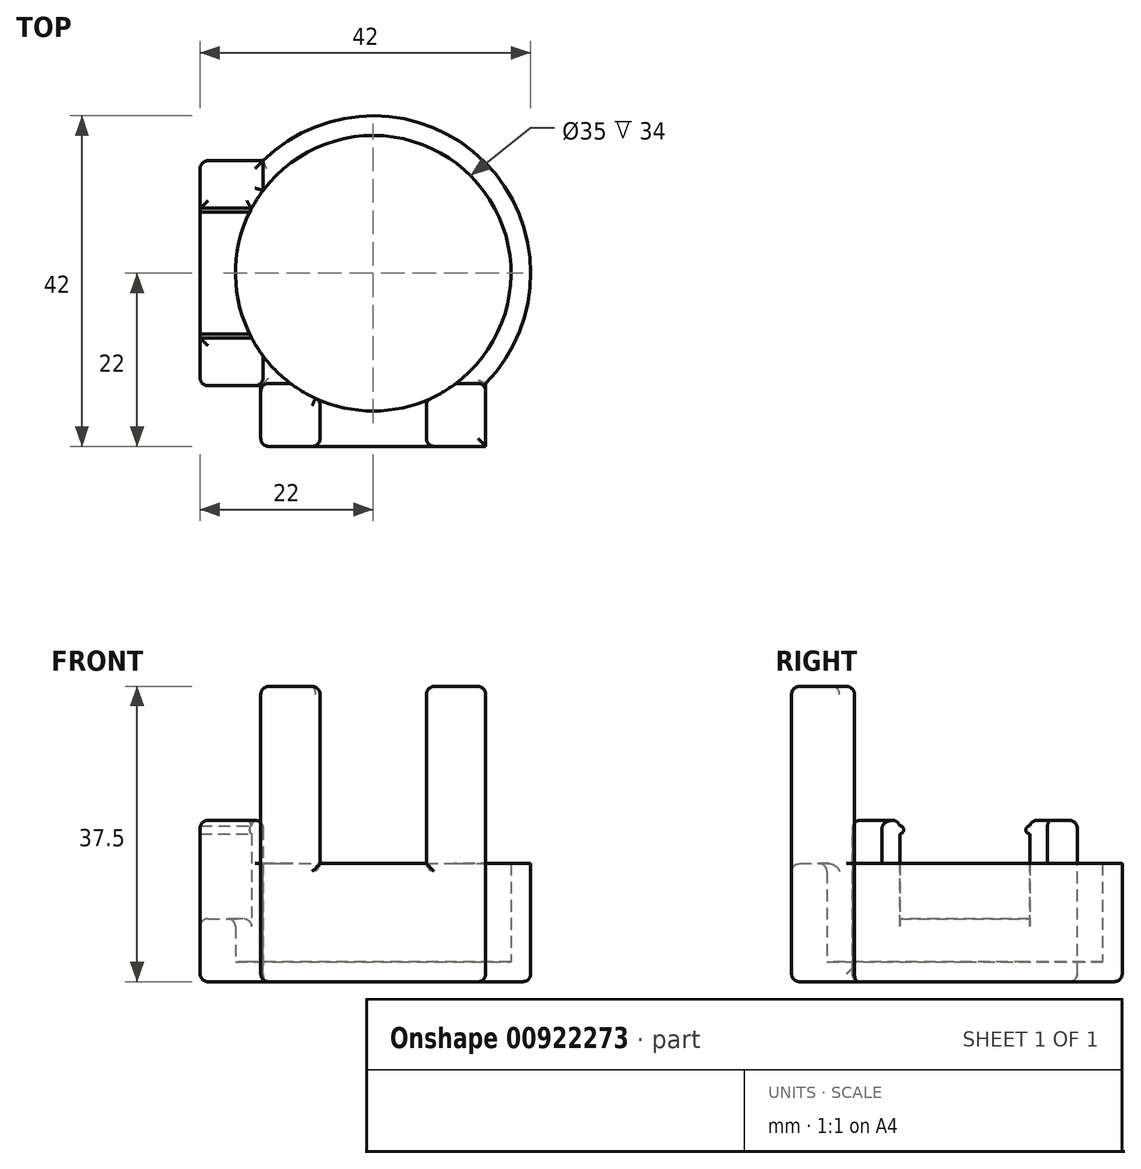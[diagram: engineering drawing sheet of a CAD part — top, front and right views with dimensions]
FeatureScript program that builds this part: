
annotation { "Feature Type Name" : "Feature", "Feature Type Description" : "" }
export const myFeature = defineFeature(function(context is Context, id is Id, definition is map)
    precondition{}
    {
        {
            var Q0;
            Q0=qCreatedBy(makeId("Top.planeOp"),FACE);
            var sketch = newSketch(context, id + "F0", { "sketchPlane" : qUnion([Q0])});
            skCircle(sketch, "E0", {"center": v(0, 0) * mm, "radius": 20 * mm});
            skSolve(sketch);
        }
        {
            var Q0;
            Q0=qSketchRegion(id+"F0",true);
            extrude(context, id + "F1", {"entities" : qUnion([Q0]), "depth" : 18 * mm, "offsetDistance" : 25 * mm});
        }
        {
            var Q0;
            Q0=makeQuery(id+"F1.opExtrude","CAP_FACE",FACE,{"disambiguationData":[OSD([sQuery(id+"F0.wireOp",EDGE,"E0")])],"isStart":true});
            extrude(context, id + "F2", {"entities" : qUnion([Q0]), "operationType" : NewBodyOperationType.ADD, "depth" : 2.5 * mm, "offsetDistance" : 25 * mm});
        }
        {
            var Q0;
            Q0=qCreatedBy(makeId("Top.planeOp"),FACE);
            var sketch = newSketch(context, id + "F3", { "sketchPlane" : qUnion([Q0])});
            skCircle(sketch, "E1", {"center": v(0, 0) * mm, "radius": 17.5 * mm});
            skSolve(sketch);
        }
        {
            var Q0;
            Q0=qCreatedBy(makeId("Front.planeOp"),FACE);
            var sketch = newSketch(context, id + "F4", { "sketchPlane" : qUnion([Q0])});
            skLineSegment(sketch, "E2.bottom", {"start": v(26, 12.5) * mm, "end": v(-14, 12.5) * mm});
            skLineSegment(sketch, "E2.top", {"start": v(26, 62.5) * mm, "end": v(-14, 62.5) * mm});
            skLineSegment(sketch, "E2.left", {"start": v(26, 12.5) * mm, "end": v(26, 62.5) * mm});
            skLineSegment(sketch, "E2.right", {"start": v(-14, 12.5) * mm, "end": v(-14, 62.5) * mm});
            skSolve(sketch);
        }
        {
            var Q0;
            Q0=qSketchRegion(id+"F4",true);
            extrude(context, id + "F5", {"entities" : qUnion([Q0]), "operationType" : NewBodyOperationType.REMOVE, "endBound" : BoundingType.SYMMETRIC, "depth" : 50 * mm, "offsetDistance" : 25 * mm});
        }
        {
            var Q0;
            Q0=qCreatedBy(makeId("Top.planeOp"),FACE);
            var sketch = newSketch(context, id + "F6", { "sketchPlane" : qUnion([Q0])});
            skLineSegment(sketch, "E3.bottom", {"start": v(-14, 14.28) * mm, "end": v(-22, 14.28) * mm});
            skLineSegment(sketch, "E3.top", {"start": v(-14, -14.28) * mm, "end": v(-22, -14.28) * mm});
            skLineSegment(sketch, "E3.left", {"start": v(-14, 14.28) * mm, "end": v(-14, -14.28) * mm});
            skLineSegment(sketch, "E3.right", {"start": v(-22, 14.28) * mm, "end": v(-22, -14.28) * mm});
            skSolve(sketch);
        }
        {
            var Q0;
            Q0=qSketchRegion(id+"F6",true);
            extrude(context, id + "F7", {"entities" : qUnion([Q0]), "operationType" : NewBodyOperationType.ADD, "oppositeDirection" : true, "depth" : 2.5 * mm, "offsetDistance" : 25 * mm});
        }
        {
            var Q0;
            Q0=qSketchRegion(id+"F6",true);
            extrude(context, id + "F8", {"entities" : qUnion([Q0]), "operationType" : NewBodyOperationType.ADD, "depth" : 18 * mm, "offsetDistance" : 25 * mm});
        }
        {
            var Q0;
            Q0=qCreatedBy(makeId("Top.planeOp"),FACE);
            var sketch = newSketch(context, id + "F9", { "sketchPlane" : qUnion([Q0])});
            skLineSegment(sketch, "E4.bottom", {"start": v(-14.28, -14) * mm, "end": v(14.28, -14) * mm});
            skLineSegment(sketch, "E4.top", {"start": v(-14.28, -22) * mm, "end": v(14.28, -22) * mm});
            skLineSegment(sketch, "E4.left", {"start": v(-14.28, -14) * mm, "end": v(-14.28, -22) * mm});
            skLineSegment(sketch, "E4.right", {"start": v(14.28, -14) * mm, "end": v(14.28, -22) * mm});
            skSolve(sketch);
        }
        {
            var Q0;
            Q0=makeQuery(id+"F9.imprint","IMPRINT",FACE,{"disambiguationData":[TD([[makeQuery(id+"F9.imprint","IMPRINT",EDGE,{"derivedFrom":sQuery(id+"F9.wireOp",EDGE,"E4.bottom")}),-1.0]])]});
            extrude(context, id + "F10", {"entities" : qUnion([Q0]), "operationType" : NewBodyOperationType.ADD, "oppositeDirection" : true, "depth" : 2.5 * mm, "offsetDistance" : 25 * mm});
        }
        {
            var Q0;
            Q0 = qSketchRegion(id + "F9", true);
            extrude(context, id + "F11", {"entities" : qUnion([Q0]), "operationType" : NewBodyOperationType.ADD, "depth" : 35 * mm, "offsetDistance" : 25 * mm});
        }
        {
            var Q0;
            Q0=qSketchRegion(id+"F3",true);
            extrude(context, id + "F12", {"entities" : qUnion([Q0]), "operationType" : NewBodyOperationType.REMOVE, "depth" : 50 * mm, "offsetDistance" : 25 * mm});
        }
        {
            var Q0;
            Q0=qCreatedBy(makeId("Right.planeOp"),FACE);
            var sketch = newSketch(context, id + "F13", { "sketchPlane" : qUnion([Q0])});
            skLineSegment(sketch, "E5.bottom", {"start": v(8.25, 50.5) * mm, "end": v(-8.25, 50.5) * mm});
            skLineSegment(sketch, "E5.top", {"start": v(8.25, 5.5) * mm, "end": v(-8.25, 5.5) * mm});
            skLineSegment(sketch, "E5.left", {"start": v(8.25, 50.5) * mm, "end": v(8.25, 5.5) * mm});
            skLineSegment(sketch, "E5.right", {"start": v(-8.25, 50.5) * mm, "end": v(-8.25, 5.5) * mm});
            skCircle(sketch, "E6", {"center": v(-8.25, 16.8) * mm, "radius": 0.5 * mm});
            skCircle(sketch, "E7", {"center": v(8.25, 16.8) * mm, "radius": 0.5 * mm});
            skSolve(sketch);
        }
        {
            var Q0;
            {var subQ4=sQuery(id+"F13.wireOp",EDGE,"E5.bottom");Q0=makeQuery(id+"F13.imprint","IMPRINT",FACE,{"disambiguationData":[TD([[makeQuery(id+"F13.imprint","IMPRINT",EDGE,{"derivedFrom":subQ4}),1.0]])]});}
            extrude(context, id + "F14", {"entities" : qUnion([Q0]), "operationType" : NewBodyOperationType.REMOVE, "oppositeDirection" : true, "depth" : 25 * mm, "offsetDistance" : 25 * mm});
        }
        {
            var Q0;
            Q0=qCreatedBy(makeId("Front.planeOp"),FACE);
            var sketch = newSketch(context, id + "F15", { "sketchPlane" : qUnion([Q0])});
            skLineSegment(sketch, "E8.bottom", {"start": v(-6.75, 37.5) * mm, "end": v(6.75, 37.5) * mm});
            skLineSegment(sketch, "E8.top", {"start": v(-6.75, 12.5) * mm, "end": v(6.75, 12.5) * mm});
            skLineSegment(sketch, "E8.left", {"start": v(-6.75, 37.5) * mm, "end": v(-6.75, 12.5) * mm});
            skLineSegment(sketch, "E8.right", {"start": v(6.75, 37.5) * mm, "end": v(6.75, 12.5) * mm});
            skSolve(sketch);
        }
        {
            var Q0;
            Q0=makeQuery(id+"F15.imprint","IMPRINT",FACE,{"disambiguationData":[TD([[makeQuery(id+"F15.imprint","IMPRINT",EDGE,{"derivedFrom":sQuery(id+"F15.wireOp",EDGE,"E8.bottom")}),-1.0]])]});
            extrude(context, id + "F16", {"entities" : qUnion([Q0]), "operationType" : NewBodyOperationType.REMOVE, "depth" : 25 * mm, "offsetDistance" : 25 * mm});
        }
        {
            var Q0;
            Q0=makeQuery(id+"F10.boolean.opBoolean","MERGE",FACE,{"derivedFrom":[makeQuery(id+"F7.boolean.opBoolean","MERGE",FACE,{"derivedFrom":[makeQuery(id+"F2.opExtrude","CAP_FACE",FACE,{"disambiguationData":[OSD([sQuery(id+"F0.wireOp",EDGE,"E0")])],"isStart":false}),makeQuery(id+"F7.opExtrude","CAP_FACE",FACE,{"disambiguationData":[OSD([sQuery(id+"F6.wireOp",EDGE,"E3.bottom"),sQuery(id+"F6.wireOp",EDGE,"E3.top"),sQuery(id+"F6.wireOp",EDGE,"E3.left"),sQuery(id+"F6.wireOp",EDGE,"E3.right")])],"isStart":false})]}),makeQuery(id+"F10.opExtrude","CAP_FACE",FACE,{"disambiguationData":[OSD([sQuery(id+"F9.wireOp",EDGE,"E4.bottom"),sQuery(id+"F9.wireOp",EDGE,"E4.top"),sQuery(id+"F9.wireOp",EDGE,"E4.left"),sQuery(id+"F9.wireOp",EDGE,"E4.right")])],"isStart":false})]});
            var Q1;
            {var subQ0=sQuery(id+"F6.wireOp",EDGE,"E3.right");var subQ1=sQuery(id+"F6.wireOp",EDGE,"E3.bottom");Q1=makeQuery(id+"F8.boolean.opBoolean","MERGE",EDGE,{"derivedFrom":[makeQuery(id+"F7.opExtrude","SWEPT_EDGE",EDGE,{"disambiguationData":[OSD([subQ1,subQ0])]}),makeQuery(id+"F8.opExtrude","SWEPT_EDGE",EDGE,{"disambiguationData":[OSD([subQ1,subQ0])]})]});}
            var Q2;
            {var subQ0=sQuery(id+"F6.wireOp",EDGE,"E3.right");var subQ2=sQuery(id+"F6.wireOp",EDGE,"E3.bottom");Q2=makeQuery(id+"F14.boolean.opBoolean","SPLIT",FACE,{"disambiguationData":[TD([makeQuery(id+"F7.opExtrude","SWEPT_FACE",FACE,{"disambiguationData":[OSD([subQ2])]})])],"derivedFrom":makeQuery(id+"F8.boolean.opBoolean","MERGE",FACE,{"derivedFrom":[makeQuery(id+"F1.opExtrude","CAP_FACE",FACE,{"disambiguationData":[OSD([sQuery(id+"F0.wireOp",EDGE,"E0")])],"isStart":false}),makeQuery(id+"F8.opExtrude","CAP_FACE",FACE,{"disambiguationData":[OSD([subQ2,sQuery(id+"F6.wireOp",EDGE,"E3.top"),sQuery(id+"F6.wireOp",EDGE,"E3.left"),subQ0])],"isStart":false})]})});}
            var Q3;
            {var subQ0=sQuery(id+"F6.wireOp",EDGE,"E3.right");var subQ1=sQuery(id+"F6.wireOp",EDGE,"E3.top");Q3=makeQuery(id+"F8.boolean.opBoolean","MERGE",EDGE,{"derivedFrom":[makeQuery(id+"F7.opExtrude","SWEPT_EDGE",EDGE,{"disambiguationData":[OSD([subQ1,subQ0])]}),makeQuery(id+"F8.opExtrude","SWEPT_EDGE",EDGE,{"disambiguationData":[OSD([subQ1,subQ0])]})]});}
            var Q4;
            {var subQ0=sQuery(id+"F6.wireOp",EDGE,"E3.right");Q4=makeQuery(id+"F14.boolean.opBoolean","INTERSECT",EDGE,{"derivedFrom":[makeQuery(id+"F8.boolean.opBoolean","MERGE",FACE,{"derivedFrom":[makeQuery(id+"F7.opExtrude","SWEPT_FACE",FACE,{"disambiguationData":[OSD([subQ0])]}),makeQuery(id+"F8.opExtrude","SWEPT_FACE",FACE,{"disambiguationData":[OSD([subQ0])]})]}),makeQuery(id+"F14.opExtrude","SWEPT_FACE",FACE,{"disambiguationData":[OSD([sQuery(id+"F13.wireOp",EDGE,"E5.top")])]})]});}
            var Q5;
            Q5=makeQuery(id+"F14.boolean.opBoolean","INTERSECT",EDGE,{"derivedFrom":[makeQuery(id+"F12.boolean.opBoolean","COPY",FACE,{"derivedFrom":makeQuery(id+"F12.opExtrude","SWEPT_FACE",FACE,{"disambiguationData":[OSD([sQuery(id+"F3.wireOp",EDGE,"E1")])]})}),makeQuery(id+"F14.opExtrude","SWEPT_FACE",FACE,{"disambiguationData":[OSD([sQuery(id+"F13.wireOp",EDGE,"E5.top")])]})]});
            fillet(context, id + "F17", {"entities" : qUnion([Q0, Q1, Q2, Q3, Q4, Q5]), "radius" : 1 * mm, "tangentPropagation" : true, "allowEdgeOverflow" : false});
        }
        {
            var Q0;
            Q0=makeQuery(id+"F11.boolean.opBoolean","SPLIT",EDGE,{"derivedFrom":makeQuery(id+"F11.opExtrude","SWEPT_EDGE",EDGE,{"disambiguationData":[OSD([sQuery(id+"F9.wireOp",EDGE,"E4.bottom"),sQuery(id+"F9.wireOp",EDGE,"E4.right")])]})});
            var Q1;
            Q1=makeQuery(id+"F12.boolean.opBoolean","INTERSECT",EDGE,{"disambiguationData":[OD(0.0)],"derivedFrom":[makeQuery(id+"F11.opExtrude","SWEPT_FACE",FACE,{"disambiguationData":[OSD([sQuery(id+"F9.wireOp",EDGE,"E4.bottom")])]}),makeQuery(id+"F12.opExtrude","SWEPT_FACE",FACE,{"disambiguationData":[OSD([sQuery(id+"F3.wireOp",EDGE,"E1")])]})]});
            var Q2;
            Q2=makeQuery(id+"F16.boolean.opBoolean","INTERSECT",EDGE,{"derivedFrom":[makeQuery(id+"F12.boolean.opBoolean","COPY",FACE,{"derivedFrom":makeQuery(id+"F12.opExtrude","SWEPT_FACE",FACE,{"disambiguationData":[OSD([sQuery(id+"F3.wireOp",EDGE,"E1")])]})}),makeQuery(id+"F16.opExtrude","SWEPT_FACE",FACE,{"disambiguationData":[OSD([sQuery(id+"F15.wireOp",EDGE,"E8.right")])]})]});
            var Q3;
            {var subQ0=sQuery(id+"F9.wireOp",EDGE,"E4.bottom");var subQ1=sQuery(id+"F9.wireOp",EDGE,"E4.top");var subQ2=sQuery(id+"F9.wireOp",EDGE,"E4.right");Q3=makeQuery(id+"F16.boolean.opBoolean","SPLIT",FACE,{"disambiguationData":[TD([makeQuery(id+"F10.opExtrude","SWEPT_FACE",FACE,{"disambiguationData":[OSD([subQ2])]})])],"derivedFrom":makeQuery(id+"F11.opExtrude","CAP_FACE",FACE,{"disambiguationData":[OSD([subQ0,subQ1,sQuery(id+"F9.wireOp",EDGE,"E4.left"),subQ2])],"isStart":false})});}
            var Q4;
            Q4=makeQuery(id+"F16.boolean.opBoolean","INTERSECT",EDGE,{"derivedFrom":[makeQuery(id+"F12.boolean.opBoolean","COPY",FACE,{"derivedFrom":makeQuery(id+"F12.opExtrude","SWEPT_FACE",FACE,{"disambiguationData":[OSD([sQuery(id+"F3.wireOp",EDGE,"E1")])]})}),makeQuery(id+"F16.opExtrude","SWEPT_FACE",FACE,{"disambiguationData":[OSD([sQuery(id+"F15.wireOp",EDGE,"E8.left")])]})]});
            var Q5;
            Q5=makeQuery(id+"F12.boolean.opBoolean","INTERSECT",EDGE,{"disambiguationData":[OD(1.0)],"derivedFrom":[makeQuery(id+"F11.opExtrude","SWEPT_FACE",FACE,{"disambiguationData":[OSD([sQuery(id+"F9.wireOp",EDGE,"E4.bottom")])]}),makeQuery(id+"F12.opExtrude","SWEPT_FACE",FACE,{"disambiguationData":[OSD([sQuery(id+"F3.wireOp",EDGE,"E1")])]})]});
            var Q6;
            Q6=makeQuery(id+"F11.opExtrude","SWEPT_EDGE",EDGE,{"disambiguationData":[OSD([sQuery(id+"F9.wireOp",EDGE,"E4.bottom"),sQuery(id+"F9.wireOp",EDGE,"E4.left")])]});
            var Q7;
            {var subQ0=sQuery(id+"F9.wireOp",EDGE,"E4.left");var subQ1=sQuery(id+"F9.wireOp",EDGE,"E4.top");Q7=makeQuery(id+"F11.boolean.opBoolean","MERGE",EDGE,{"derivedFrom":[makeQuery(id+"F10.opExtrude","SWEPT_EDGE",EDGE,{"disambiguationData":[OSD([subQ1,subQ0])]}),makeQuery(id+"F11.opExtrude","SWEPT_EDGE",EDGE,{"disambiguationData":[OSD([subQ1,subQ0])]})]});}
            var Q8;
            {var subQ0=sQuery(id+"F9.wireOp",EDGE,"E4.top");var subQ1=sQuery(id+"F9.wireOp",EDGE,"E4.bottom");var subQ2=sQuery(id+"F9.wireOp",EDGE,"E4.left");Q8=makeQuery(id+"F16.boolean.opBoolean","SPLIT",FACE,{"disambiguationData":[TD([makeQuery(id+"F10.opExtrude","SWEPT_FACE",FACE,{"disambiguationData":[OSD([subQ2])]})])],"derivedFrom":makeQuery(id+"F11.opExtrude","CAP_FACE",FACE,{"disambiguationData":[OSD([subQ1,subQ0,subQ2,sQuery(id+"F9.wireOp",EDGE,"E4.right")])],"isStart":false})});}
            var Q9;
            {var subQ0=sQuery(id+"F9.wireOp",EDGE,"E4.top");Q9=makeQuery(id+"F16.boolean.opBoolean","INTERSECT",EDGE,{"derivedFrom":[makeQuery(id+"F11.boolean.opBoolean","MERGE",FACE,{"derivedFrom":[makeQuery(id+"F10.opExtrude","SWEPT_FACE",FACE,{"disambiguationData":[OSD([subQ0])]}),makeQuery(id+"F11.opExtrude","SWEPT_FACE",FACE,{"disambiguationData":[OSD([subQ0])]})]}),makeQuery(id+"F16.opExtrude","SWEPT_FACE",FACE,{"disambiguationData":[OSD([sQuery(id+"F15.wireOp",EDGE,"E8.left")])]})]});}
            var Q10;
            {var subQ0=sQuery(id+"F9.wireOp",EDGE,"E4.top");Q10=makeQuery(id+"F16.boolean.opBoolean","INTERSECT",EDGE,{"derivedFrom":[makeQuery(id+"F11.boolean.opBoolean","MERGE",FACE,{"derivedFrom":[makeQuery(id+"F10.opExtrude","SWEPT_FACE",FACE,{"disambiguationData":[OSD([subQ0])]}),makeQuery(id+"F11.opExtrude","SWEPT_FACE",FACE,{"disambiguationData":[OSD([subQ0])]})]}),makeQuery(id+"F16.opExtrude","SWEPT_FACE",FACE,{"disambiguationData":[OSD([sQuery(id+"F15.wireOp",EDGE,"E8.right")])]})]});}
            var Q11;
            {var subQ0=sQuery(id+"F9.wireOp",EDGE,"E4.top");Q11=makeQuery(id+"F16.boolean.opBoolean","INTERSECT",EDGE,{"derivedFrom":[makeQuery(id+"F11.boolean.opBoolean","MERGE",FACE,{"derivedFrom":[makeQuery(id+"F10.opExtrude","SWEPT_FACE",FACE,{"disambiguationData":[OSD([subQ0])]}),makeQuery(id+"F11.opExtrude","SWEPT_FACE",FACE,{"disambiguationData":[OSD([subQ0])]})]}),makeQuery(id+"F16.opExtrude","SWEPT_FACE",FACE,{"disambiguationData":[OSD([sQuery(id+"F15.wireOp",EDGE,"E8.top")])]})]});}
            var Q12;
            Q12=makeQuery(id+"F16.boolean.opBoolean","INTERSECT",EDGE,{"derivedFrom":[makeQuery(id+"F12.boolean.opBoolean","COPY",FACE,{"derivedFrom":makeQuery(id+"F12.opExtrude","SWEPT_FACE",FACE,{"disambiguationData":[OSD([sQuery(id+"F3.wireOp",EDGE,"E1")])]})}),makeQuery(id+"F16.opExtrude","SWEPT_FACE",FACE,{"disambiguationData":[OSD([sQuery(id+"F15.wireOp",EDGE,"E8.top")])]})]});
            fillet(context, id + "F18", {"entities" : qUnion([Q0, Q1, Q2, Q3, Q4, Q5, Q6, Q7, Q8, Q9, Q10, Q11, Q12]), "radius" : 1 * mm, "tangentPropagation" : true, "allowEdgeOverflow" : false});
        }
        {
            var Q0;
            {var subQ0=sQuery(id+"F6.wireOp",EDGE,"E3.right");var subQ1=sQuery(id+"F6.wireOp",EDGE,"E3.top");Q0=makeQuery(id+"F14.boolean.opBoolean","SPLIT",EDGE,{"disambiguationData":[TD([makeQuery(id+"F7.opExtrude","SWEPT_FACE",FACE,{"disambiguationData":[OSD([subQ1])]})])],"derivedFrom":makeQuery(id+"F8.opExtrude","CAP_EDGE",EDGE,{"disambiguationData":[OSD([subQ0])],"isStart":false})});}
            var Q1;
            {var subQ0=sQuery(id+"F13.wireOp",EDGE,"E5.right");Q1=makeQuery(id+"F14.boolean.opBoolean","INTERSECT",EDGE,{"derivedFrom":[makeQuery(id+"F8.boolean.opBoolean","MERGE",FACE,{"derivedFrom":[makeQuery(id+"F1.opExtrude","CAP_FACE",FACE,{"disambiguationData":[OSD([sQuery(id+"F0.wireOp",EDGE,"E0")])],"isStart":false}),makeQuery(id+"F8.opExtrude","CAP_FACE",FACE,{"disambiguationData":[OSD([sQuery(id+"F6.wireOp",EDGE,"E3.bottom"),sQuery(id+"F6.wireOp",EDGE,"E3.top"),sQuery(id+"F6.wireOp",EDGE,"E3.left"),sQuery(id+"F6.wireOp",EDGE,"E3.right")])],"isStart":false})]}),makeQuery(id+"F14.opExtrude","SWEPT_FACE",FACE,{"disambiguationData":[OSD([subQ0]),TDD([makeQuery(id+"F13.imprint","IMPRINT",EDGE,{"disambiguationData":[TD([[makeQuery(id+"F13.imprint","INTERSECT",VERTEX,{"derivedFrom":[sQuery(id+"F13.wireOp",EDGE,"E5.bottom"),subQ0]}),-1.0]])],"derivedFrom":subQ0})])]})]});}
            var Q2;
            {var subQ0=makeQuery(id+"F5.opExtrude","SWEPT_FACE",FACE,{"disambiguationData":[OSD([sQuery(id+"F4.wireOp",EDGE,"E2.right")])]});var subQ1=makeQuery(id+"F1.opExtrude","CAP_FACE",FACE,{"disambiguationData":[OSD([sQuery(id+"F0.wireOp",EDGE,"E0")])],"isStart":false});Q2=makeQuery(id+"F12.boolean.opBoolean","SPLIT",EDGE,{"disambiguationData":[TD([makeQuery(id+"F11.opExtrude","SWEPT_FACE",FACE,{"disambiguationData":[OSD([sQuery(id+"F9.wireOp",EDGE,"E4.bottom")])]})])],"derivedFrom":makeQuery(id+"F5.boolean.opBoolean","INTERSECT",EDGE,{"derivedFrom":[subQ1,subQ0]})});}
            var Q3;
            {var subQ0=makeQuery(id+"F11.opExtrude","SWEPT_FACE",FACE,{"disambiguationData":[OSD([sQuery(id+"F9.wireOp",EDGE,"E4.bottom")])]});var subQ1=sQuery(id+"F6.wireOp",EDGE,"E3.top");var subQ2=makeQuery(id+"F8.boolean.opBoolean","MERGE",FACE,{"derivedFrom":[makeQuery(id+"F1.opExtrude","CAP_FACE",FACE,{"disambiguationData":[OSD([sQuery(id+"F0.wireOp",EDGE,"E0")])],"isStart":false}),makeQuery(id+"F8.opExtrude","CAP_FACE",FACE,{"disambiguationData":[OSD([sQuery(id+"F6.wireOp",EDGE,"E3.bottom"),subQ1,sQuery(id+"F6.wireOp",EDGE,"E3.left"),sQuery(id+"F6.wireOp",EDGE,"E3.right")])],"isStart":false})]});var subQ3=makeQuery(id+"F5.boolean.opBoolean","COPY",FACE,{"derivedFrom":makeQuery(id+"F5.opExtrude","SWEPT_FACE",FACE,{"disambiguationData":[OSD([sQuery(id+"F4.wireOp",EDGE,"E2.right")])]})});Q3=makeQuery(id+"F18.opFillet","TWEAK_EDGE",EDGE,{"disambiguationData":[OD(0.0)],"derivedFrom":[makeQuery(id+"F11.boolean.opBoolean","INTERSECT",VERTEX,{"derivedFrom":[subQ2,makeQuery(id+"F8.boolean.opBoolean","MERGE",FACE,{"derivedFrom":[makeQuery(id+"F7.opExtrude","SWEPT_FACE",FACE,{"disambiguationData":[OSD([subQ1])]}),makeQuery(id+"F8.opExtrude","SWEPT_FACE",FACE,{"disambiguationData":[OSD([subQ1])]})]}),makeQuery(id+"F11.opExtrude","SWEPT_FACE",FACE,{"disambiguationData":[OSD([sQuery(id+"F9.wireOp",EDGE,"E4.left")])]})]}),makeQuery(id+"F11.boolean.opBoolean","INTERSECT",VERTEX,{"derivedFrom":[makeQuery(id+"F5.boolean.opBoolean","COPY",FACE,{"derivedFrom":makeQuery(id+"F5.opExtrude","SWEPT_FACE",FACE,{"disambiguationData":[OSD([sQuery(id+"F4.wireOp",EDGE,"E2.bottom")])]})}),subQ3,subQ0]}),makeQuery(id+"F11.boolean.opBoolean","INTERSECT",VERTEX,{"derivedFrom":[subQ3,subQ2,subQ0]})]});}
            fillet(context, id + "F19", {"entities" : qUnion([Q0, Q1, Q2, Q3]), "radius" : 1 * mm, "tangentPropagation" : true, "allowEdgeOverflow" : false});
        }
    });
